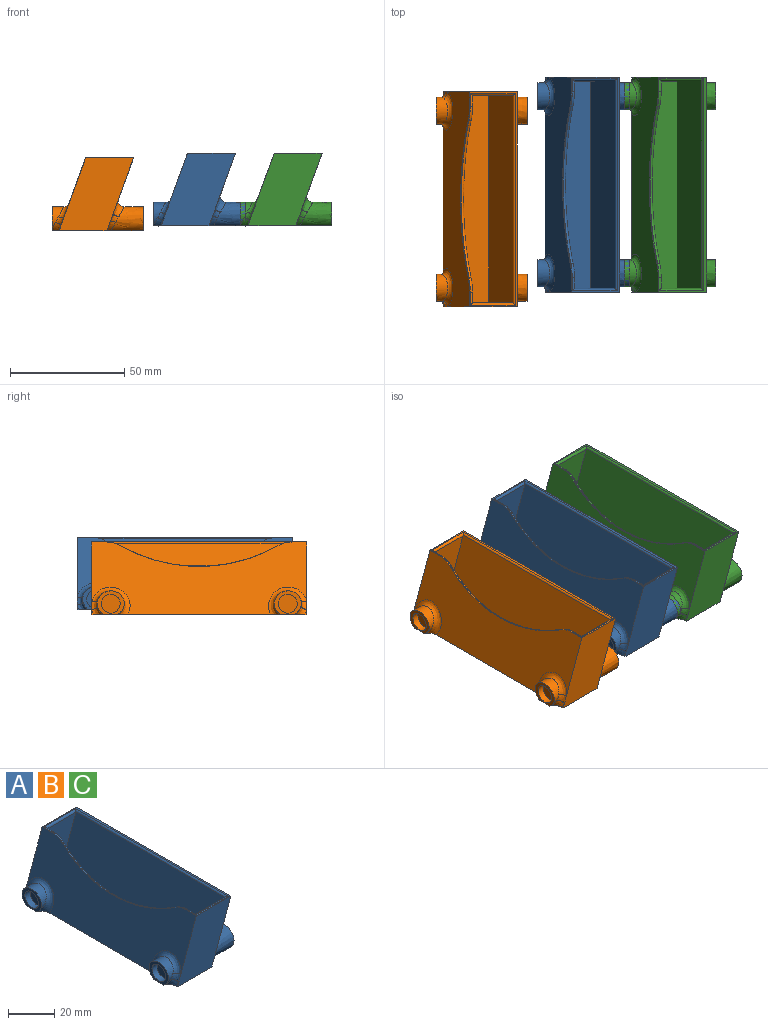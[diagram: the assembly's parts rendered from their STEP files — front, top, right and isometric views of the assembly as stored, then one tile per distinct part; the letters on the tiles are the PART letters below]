
ASSEMBLY  parts=3 mates=1
PART A: 55 faces, bbox 41.3x95.1x36.1 mm
  f0: plane 93.99x31.76mm, normal (0.94,0,-0.34), area 2754.9mm2, adj f5,f7,f8,f9,f49,f54
  f1: plane 3.89x2.2mm, normal (0.94,0,-0.34), area 3.5mm2, adj f7,f9,f52
  f2: plane 3.89x2.19mm, normal (0.94,0,-0.34), area 3.5mm2, adj f8,f9,f51
  f3: plane 93.99x31.76mm, normal (-0.94,0,0.34), area 2237.6mm2, adj f5,f7,f8,f9,f15,f16,f17,f18
  f4: plane 2.15x0.85mm, normal (-0.94,0,0.34), area 0.8mm2, adj f8,f9,f40
  f5: plane 93.98x20.96mm, normal (0,0,1), area 120.6mm2, adj f0,f3,f7,f8,f16,f17,f19,f21
  f6: plane 2.15x0.85mm, normal (-0.94,0,0.34), area 0.8mm2, adj f7,f9,f35
  f7: plane 32.52x31.76mm, normal (0,-1,0), area 665.3mm2, adj f0,f1,f3,f5,f6,f9,f36,f53
  f8: plane 32.52x31.76mm, normal (0,1,0), area 665.3mm2, adj f0,f2,f3,f4,f5,f9,f39,f50
  f9: plane 94.7x40.67mm, normal (0,0,-1), area 2221.8mm2, adj f0,f1,f2,f3,f4,f6,f7,f8
  f10: plane 29.17x28.19mm, normal (0,1,0), area 512.7mm2, adj f12,f13,f14,f25,f26
  f11: plane 29.17x28.19mm, normal (0,-1,0), area 512.7mm2, adj f12,f13,f14,f19,f21
  f12: plane 90.81x17.58mm, normal (0,0,1), area 1596mm2, adj f10,f11,f13,f14
  f13: plane 90.93x29.51mm, normal (-0.94,0,0.34), area 2851.7mm2, adj f10,f11,f12,f21,f23,f25
  f14: plane 90.81x28.83mm, normal (0.94,0,-0.34), area 2207.1mm2, adj f10,f11,f12,f19,f20,f22,f24,f26
  f15: plane 12.19x0.27mm, normal (1,0,0), area 2.2mm2, adj f3,f18
  f16: cylinder r=12.7mm len=6.25mm, axis (-1,0,0), area 1.3mm2, adj f3,f5,f18,f20
  f17: cylinder r=12.7mm len=6.25mm, axis (-1,0,0), area 1.3mm2, adj f3,f5,f18,f24
  f18: cylinder r=69.85mm len=68.78mm, axis (-1,0,0), area 20.1mm2, adj f3,f15,f16,f17,f22
  f19: cylinder r=0.99mm len=5.75mm, axis (0,-1,0), area 9.6mm2, adj f5,f11,f14,f20,f21
  f20: bspline ~9.34x3.15mm, area 12.1mm2, adj f14,f16,f19,f22
  f21: cylinder r=0.99mm len=19.68mm, axis (-1,0,0), area 28.7mm2, adj f5,f11,f13,f19,f23
  f22: bspline ~69.75x10.38mm, area 136.9mm2, adj f14,f18,f20,f24
  f23: cylinder r=0.99mm len=92.79mm, axis (0,1,0), area 111.2mm2, adj f5,f13,f21,f25
  f24: bspline ~7.62x3.15mm, area 12.1mm2, adj f14,f17,f22,f26
  f25: cylinder r=0.99mm len=19.68mm, axis (1,0,0), area 28.7mm2, adj f5,f10,f13,f23,f26
  f26: cylinder r=0.99mm len=5.75mm, axis (0,-1,0), area 9.6mm2, adj f5,f10,f14,f24,f25
  f27: extruded ~11.81x9.6mm, area 82.7mm2, adj f30,f38,f39,f40
  f28: extruded ~11.81x9.6mm, area 82.7mm2, adj f33,f35,f36,f37
  f29: cylinder r=4.14mm len=8.28mm, axis (1,0,0), area 81.3mm2, adj f30,f31
  f30: plane 11.87x10.37mm, normal (-1,0,0), area 46.3mm2, adj f9,f27,f29,f38,f40
  f31: plane 8.28x8.28mm, normal (-1,0,0), area 53.9mm2, adj f29
  f32: cylinder r=4.14mm len=8.28mm, axis (1,0,0), area 81.3mm2, adj f33,f34
  f33: plane 11.87x10.37mm, normal (-1,0,0), area 46.3mm2, adj f9,f28,f32,f35,f37
  f34: plane 8.28x8.28mm, normal (-1,0,0), area 53.9mm2, adj f32
  f35: bspline ~7.78x6.4mm, area 16.5mm2, adj f6,f9,f28,f33,f36
  f36: bspline ~4.89x4.13mm, area 11.8mm2, adj f7,f28,f35,f37
  f37: bspline ~16.93x15.37mm, area 92.8mm2, adj f3,f9,f28,f33,f36
  f38: bspline ~16.88x15.59mm, area 92.8mm2, adj f3,f9,f27,f30,f39
  f39: bspline ~4.55x3.97mm, area 11.8mm2, adj f8,f27,f38,f40
  f40: bspline ~7.83x6.62mm, area 16.5mm2, adj f4,f9,f27,f30,f39
  f41: plane 11.84x10.34mm, normal (1,0,0), area 46.3mm2, adj f9,f42,f47
  f42: extruded ~13.98x11.82mm, area 321.6mm2, adj f9,f41,f52,f53,f54
  f43: plane 11.84x10.34mm, normal (1,0,0), area 46.3mm2, adj f9,f44,f45
  f44: extruded ~13.98x11.82mm, area 321.6mm2, adj f9,f43,f49,f50,f51
  f45: cylinder r=4.14mm len=8.28mm, axis (1,0,0), area 81.3mm2, adj f43,f46
  f46: plane 8.28x8.28mm, normal (1,0,0), area 53.9mm2, adj f45
  f47: cylinder r=4.14mm len=8.28mm, axis (1,0,0), area 81.3mm2, adj f41,f48
  f48: plane 8.28x8.28mm, normal (1,0,0), area 53.9mm2, adj f47
  f49: bspline ~16.93x15.44mm, area 114.1mm2, adj f0,f9,f44,f50
  f50: bspline ~4.89x4.13mm, area 11.8mm2, adj f8,f44,f49,f51
  f51: bspline ~7.27x5.85mm, area 16.9mm2, adj f2,f9,f44,f50
  f52: bspline ~6.4x5.82mm, area 16.9mm2, adj f1,f9,f42,f53
  f53: bspline ~4.55x3.97mm, area 11.8mm2, adj f7,f42,f52,f54
  f54: bspline ~16.93x15.41mm, area 114.9mm2, adj f0,f9,f42,f53
PART B: same geometry as A
PART C: same geometry as A
PLACE A t=(-32.48,7.8,-7.73)mm
PLACE B t=(-77.08,1.45,-9.75)mm
PLACE C t=(5.44,7.8,-7.73)mm
MATE slider A.f41 <-> C.f33  axis (1,0,0) through (-14.06,-30.93,-2.63)mm
